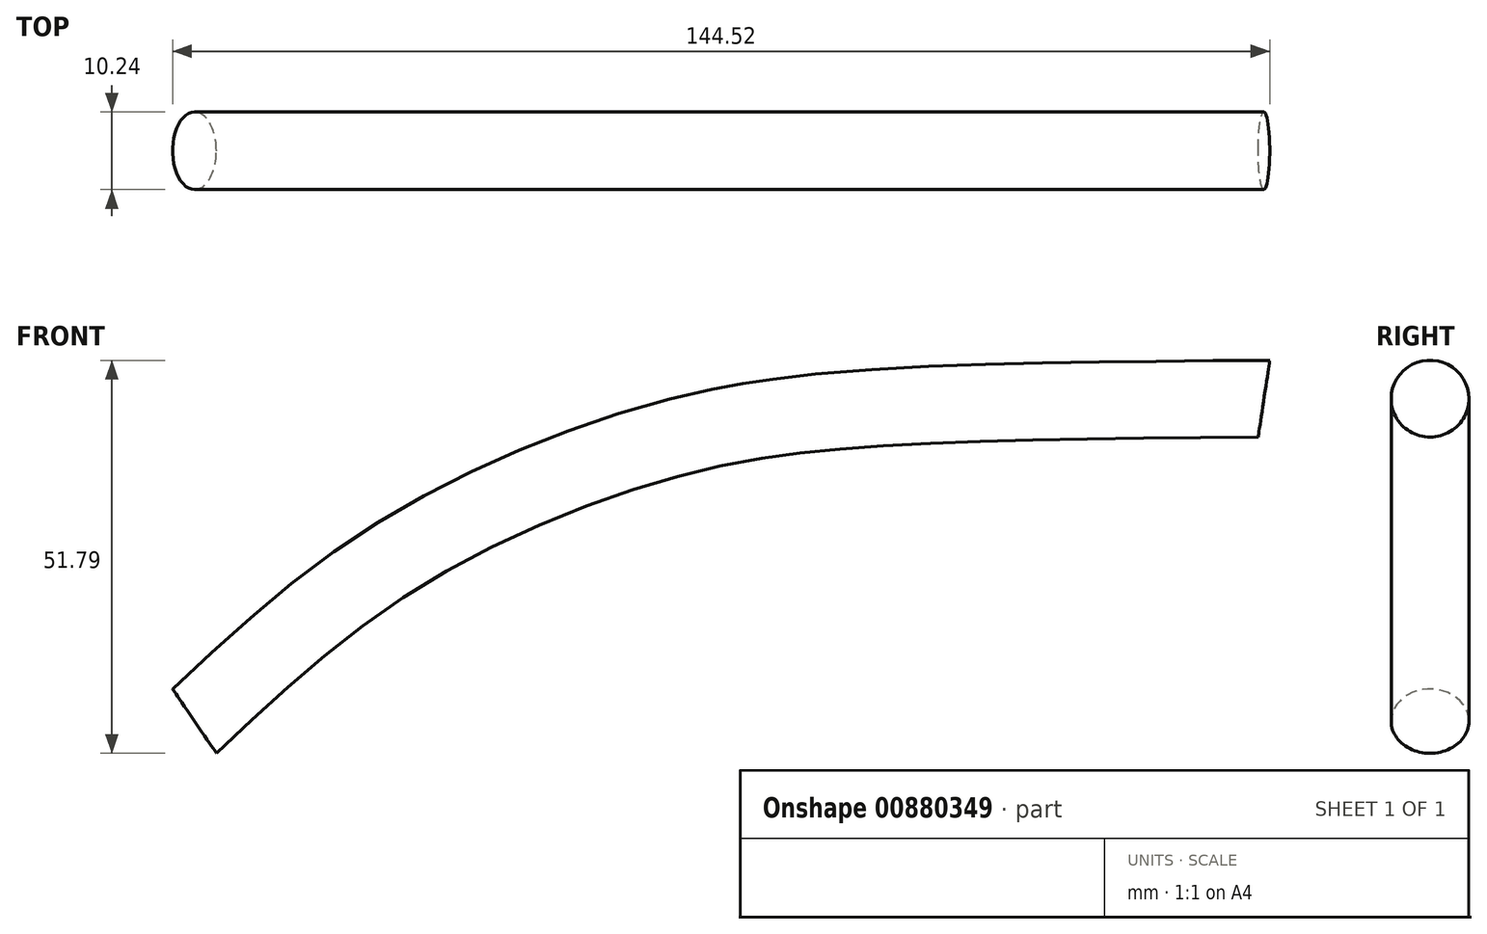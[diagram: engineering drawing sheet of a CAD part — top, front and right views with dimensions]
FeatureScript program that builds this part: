
annotation { "Feature Type Name" : "Feature", "Feature Type Description" : "" }
export const myFeature = defineFeature(function(context is Context, id is Id, definition is map)
    precondition{}
    {
        {
            var Q0;
            Q0=qCreatedBy(makeId("Front.planeOp"),FACE);
            var sketch = newSketch(context, id + "F0", { "sketchPlane" : qUnion([Q0])});
            skFitSpline(sketch, "E0", {"points": [v(-73.93, 0) * mm, v(-48.06, 21.3) * mm, v(-14.58, 36.27) * mm, v(14.33, 41.09) * mm, v(66.32, 42.36) * mm], "startDerivative": vector(101.48, 95.28) * mm, "endDerivative": vector(191.1, 1.4) * mm});
            skSolve(sketch);
        }
        {
            var Q0;
            Q0=qCreatedBy(makeId("Right.planeOp"),FACE);
            var sketch = newSketch(context, id + "F1", { "sketchPlane" : qUnion([Q0])});
            skCircle(sketch, "E1", {"center": v(0, 40.44) * mm, "radius": 5.12 * mm});
            skSolve(sketch);
        }
        {
            var Q0;
            Q0=makeQuery(id+"F1.imprint","IMPRINT",FACE,{"disambiguationData":[TD([[makeQuery(id+"F1.imprint","IMPRINT",EDGE,{"derivedFrom":sQuery(id+"F1.wireOp",EDGE,"E1")}),1.0]])]});
            var Q1;
            Q1=sQuery(id+"F0.wireOp",EDGE,"E0");
            sweep(context, id + "F2", {"profiles" : qUnion([Q0]), "path" : qUnion([Q1])});
        }
    });
